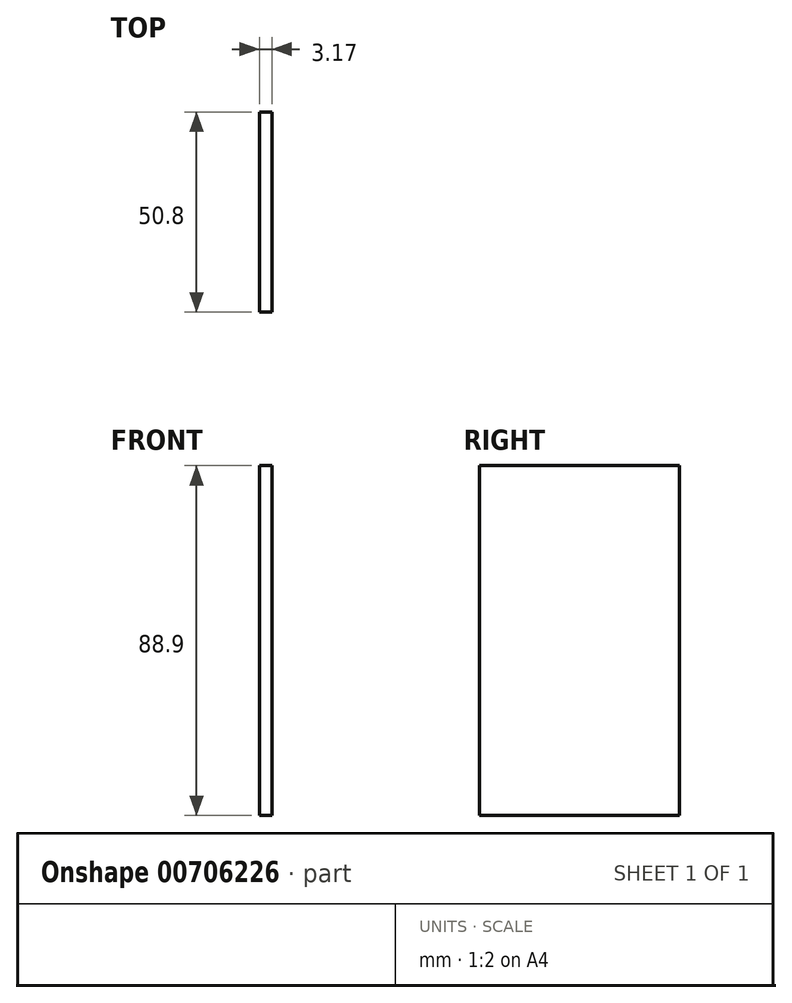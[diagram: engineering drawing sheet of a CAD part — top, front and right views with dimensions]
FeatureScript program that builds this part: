
annotation { "Feature Type Name" : "Feature", "Feature Type Description" : "" }
export const myFeature = defineFeature(function(context is Context, id is Id, definition is map)
    precondition{}
    {
        {
            var Q0;
            Q0=qCreatedBy(makeId("Right.planeOp"),FACE);
            var sketch = newSketch(context, id + "F0", { "sketchPlane" : qUnion([Q0])});
            skLineSegment(sketch, "E0.bottom", {"start": v(-23, 33.78) * mm, "end": v(27.8, 33.78) * mm});
            skLineSegment(sketch, "E0.top", {"start": v(-23, -55.12) * mm, "end": v(27.8, -55.12) * mm});
            skLineSegment(sketch, "E0.left", {"start": v(-23, 33.78) * mm, "end": v(-23, -55.12) * mm});
            skLineSegment(sketch, "E0.right", {"start": v(27.8, 33.78) * mm, "end": v(27.8, -55.12) * mm});
            skSolve(sketch);
        }
        {
            var Q0;
            Q0=qSketchRegion(id+"F0",true);
            extrude(context, id + "F1", {"entities" : qUnion([Q0]), "depth" : 3.17 * mm, "offsetDistance" : 25.4 * mm});
        }
    });
